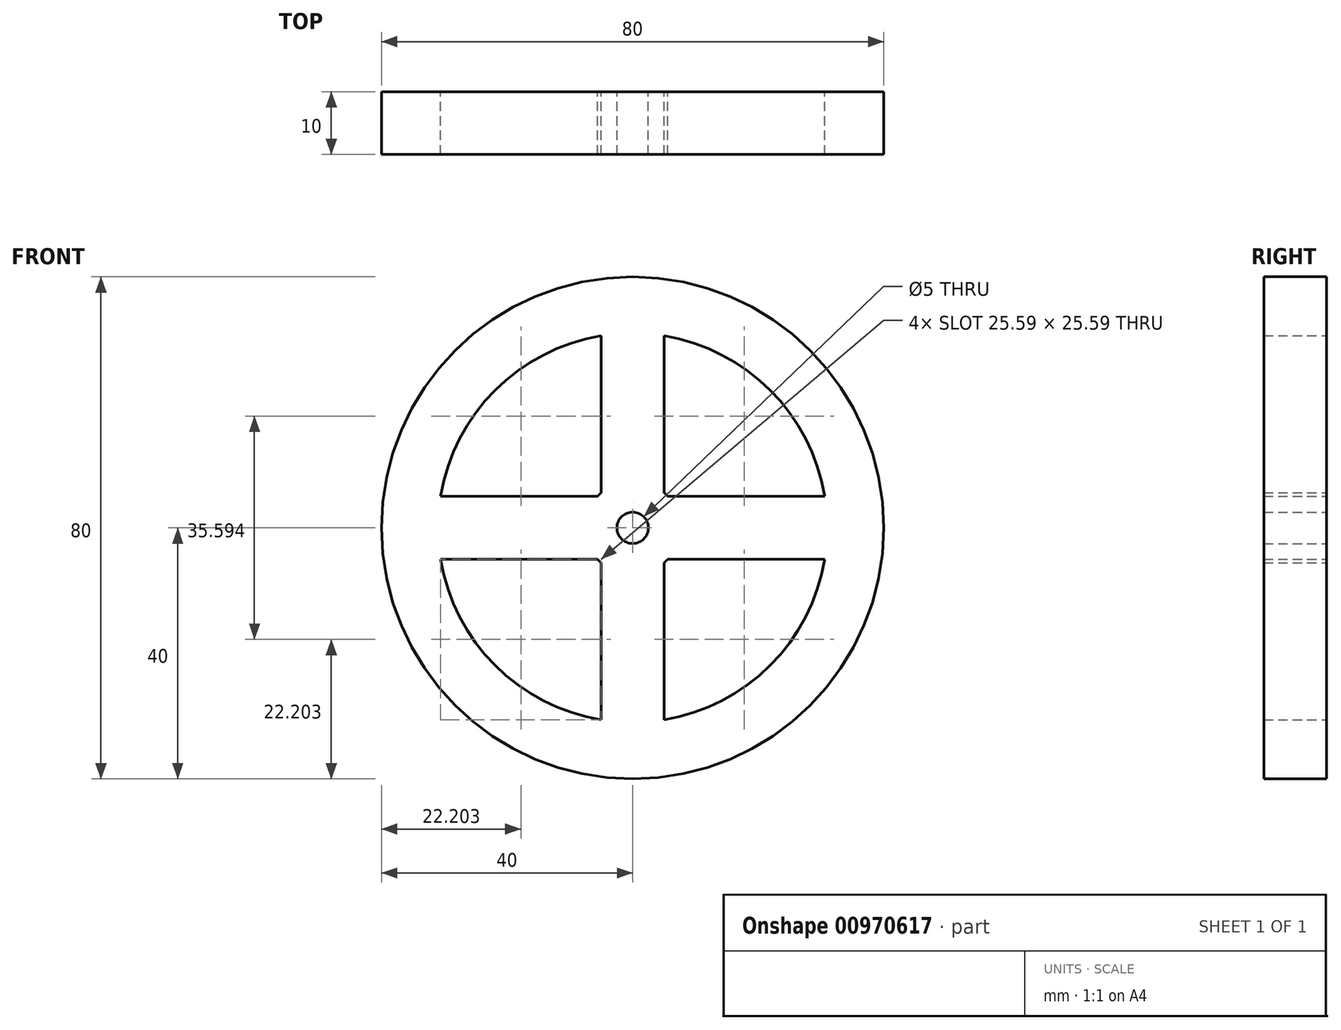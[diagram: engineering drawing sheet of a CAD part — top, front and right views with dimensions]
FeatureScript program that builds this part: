
annotation { "Feature Type Name" : "Feature", "Feature Type Description" : "" }
export const myFeature = defineFeature(function(context is Context, id is Id, definition is map)
    precondition{}
    {
        {
            var Q0;
            Q0=qCreatedBy(makeId("Front.planeOp"),FACE);
            var sketch = newSketch(context, id + "F0", { "sketchPlane" : qUnion([Q0])});
            skCircle(sketch, "E0", {"center": v(0, 0) * mm, "radius": 40 * mm});
            skArc(sketch, "E1", {"start": v(-30.6, -5) * mm, "mid": v(-21.92, -21.92) * mm, "end": v(-5, -30.6) * mm});
            skArc(sketch, "E2", {"start": v(-5, 5.6) * mm, "mid": v(-5.3, 5.3) * mm, "end": v(-5.6, 5) * mm});
            skCircle(sketch, "E3", {"center": v(0, 0) * mm, "radius": 2.5 * mm});
            skLineSegment(sketch, "E4", {"start": v(0, 2.5) * mm, "end": v(0, 31) * mm, "construction": true});
            skLineSegment(sketch, "E5", {"start": v(2.5, 0) * mm, "end": v(31, 0) * mm, "construction": true});
            skLineSegment(sketch, "E6", {"start": v(0, -2.5) * mm, "end": v(0, -31) * mm, "construction": true});
            skLineSegment(sketch, "E7", {"start": v(-2.5, 0) * mm, "end": v(-31, 0) * mm, "construction": true});
            skLineSegment(sketch, "E8.0", {"start": v(5, 5.6) * mm, "end": v(5, 30.6) * mm});
            skLineSegment(sketch, "E9.0", {"start": v(-5, 5.6) * mm, "end": v(-5, 30.6) * mm});
            skLineSegment(sketch, "E10.0", {"start": v(5.6, -5) * mm, "end": v(30.6, -5) * mm});
            skLineSegment(sketch, "E11.0", {"start": v(5.6, 5) * mm, "end": v(30.6, 5) * mm});
            skLineSegment(sketch, "E12.0", {"start": v(-5, -5.6) * mm, "end": v(-5, -30.6) * mm});
            skLineSegment(sketch, "E13.0", {"start": v(5, -5.6) * mm, "end": v(5, -30.6) * mm});
            skLineSegment(sketch, "E14.0", {"start": v(-5.6, 5) * mm, "end": v(-30.6, 5) * mm});
            skLineSegment(sketch, "E15.0", {"start": v(-5.6, -5) * mm, "end": v(-30.6, -5) * mm});
            skArc(sketch, "E16.trimOffspring", {"start": v(5.6, 5) * mm, "mid": v(5.3, 5.3) * mm, "end": v(5, 5.6) * mm});
            skArc(sketch, "E17.trimOffspring", {"start": v(5, -5.6) * mm, "mid": v(5.3, -5.3) * mm, "end": v(5.6, -5) * mm});
            skArc(sketch, "E18.trimOffspring", {"start": v(-5.6, -5) * mm, "mid": v(-5.3, -5.3) * mm, "end": v(-5, -5.6) * mm});
            skArc(sketch, "E19.trimOffspring", {"start": v(5, -30.6) * mm, "mid": v(21.92, -21.92) * mm, "end": v(30.6, -5) * mm});
            skArc(sketch, "E20.trimOffspring", {"start": v(30.6, 5) * mm, "mid": v(21.92, 21.92) * mm, "end": v(5, 30.6) * mm});
            skArc(sketch, "E21.trimOffspring", {"start": v(-5, 30.6) * mm, "mid": v(-21.92, 21.92) * mm, "end": v(-30.6, 5) * mm});
            skSolve(sketch);
        }
        {
            var Q0;
            Q0=makeQuery(id+"F0.imprint","IMPRINT",FACE,{"disambiguationData":[TD([[makeQuery(id+"F0.imprint","IMPRINT",EDGE,{"derivedFrom":sQuery(id+"F0.wireOp",EDGE,"E0")}),1.0]])]});
            extrude(context, id + "F1", {"entities" : qUnion([Q0]), "endBound" : BoundingType.SYMMETRIC, "depth" : 10 * mm, "offsetDistance" : 25 * mm});
        }
    });
